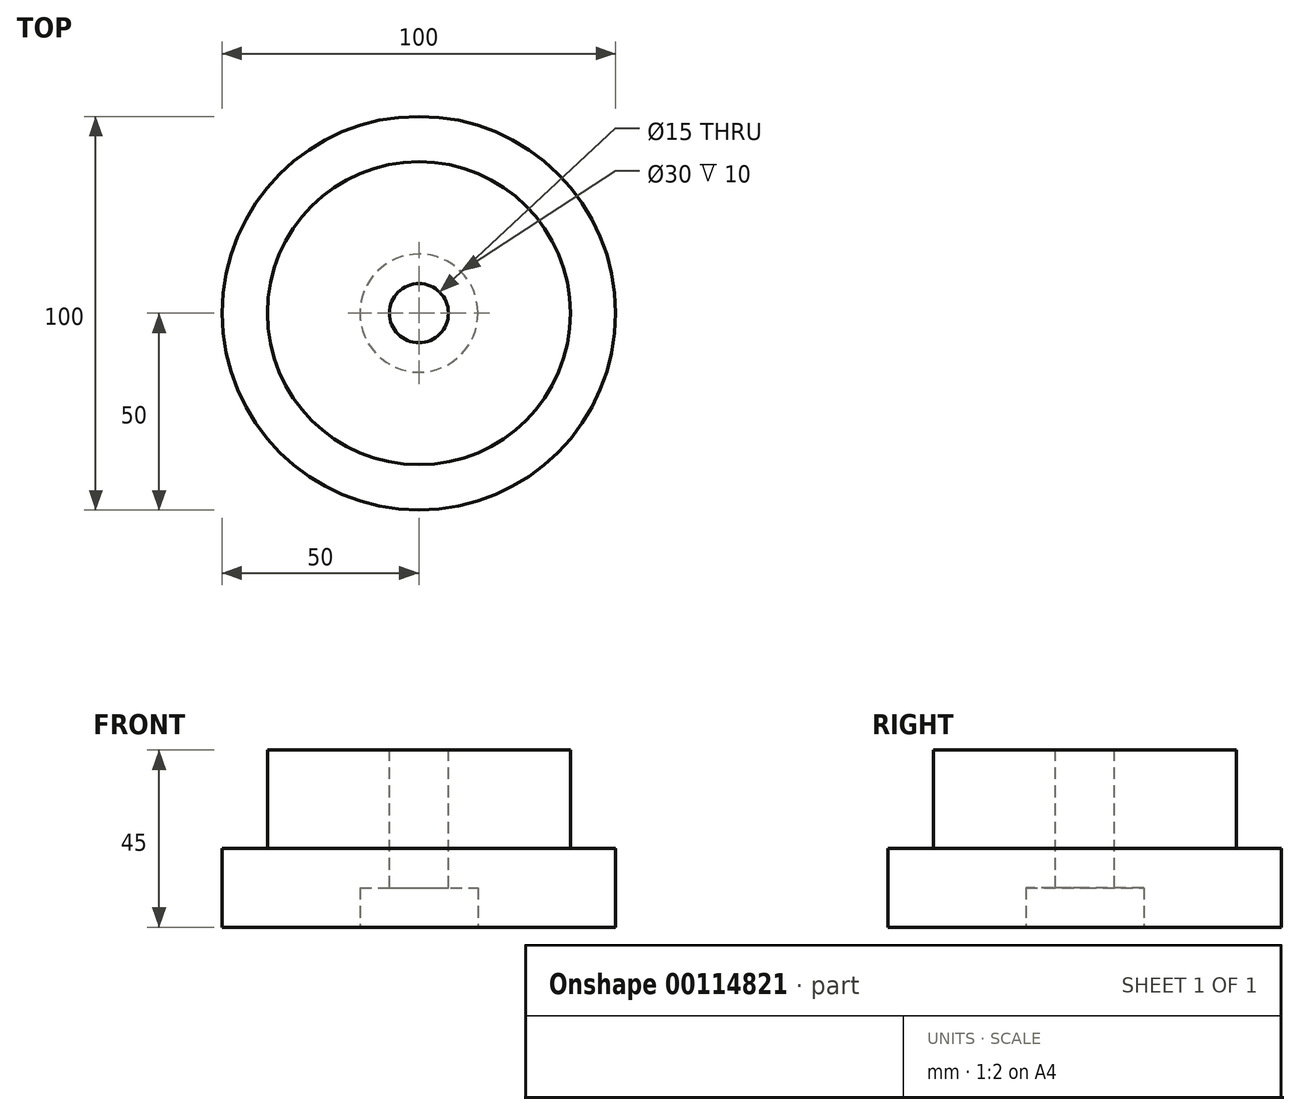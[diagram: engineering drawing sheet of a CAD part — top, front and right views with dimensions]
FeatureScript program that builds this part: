
annotation { "Feature Type Name" : "Feature", "Feature Type Description" : "" }
export const myFeature = defineFeature(function(context is Context, id is Id, definition is map)
    precondition{}
    {
        {
            var Q0;
            Q0=qCreatedBy(makeId("Top.planeOp"),FACE);
            var sketch = newSketch(context, id + "F0", { "sketchPlane" : qUnion([Q0])});
            skCircle(sketch, "E0", {"center": v(0, 0) * mm, "radius": 50 * mm});
            skSolve(sketch);
        }
        {
            var Q0;
            Q0=makeQuery(id+"F0.imprint","IMPRINT",FACE,{"disambiguationData":[TD([[makeQuery(id+"F0.imprint","IMPRINT",EDGE,{"derivedFrom":sQuery(id+"F0.wireOp",EDGE,"E0")}),1.0]])]});
            extrude(context, id + "F1", {"entities" : qUnion([Q0]), "depth" : 20 * mm});
        }
        {
            var Q0;
            Q0=makeQuery(id+"F1.opExtrude","CAP_FACE",FACE,{"disambiguationData":[OSD([sQuery(id+"F0.wireOp",EDGE,"E0")])],"isStart":false});
            var sketch = newSketch(context, id + "F2", { "sketchPlane" : qUnion([Q0])});
            skCircle(sketch, "E1", {"center": v(0, 0) * mm, "radius": 38.5 * mm});
            skSolve(sketch);
        }
        {
            var Q0;
            Q0=makeQuery(id+"F2.imprint","IMPRINT",FACE,{"disambiguationData":[TD([[makeQuery(id+"F2.imprint","IMPRINT",EDGE,{"derivedFrom":sQuery(id+"F2.wireOp",EDGE,"E1")}),1.0]])]});
            extrude(context, id + "F3", {"entities" : qUnion([Q0]), "operationType" : NewBodyOperationType.ADD, "depth" : 25 * mm});
        }
        {
            var Q0;
            Q0=makeQuery(id+"F1.opExtrude","CAP_FACE",FACE,{"disambiguationData":[OSD([sQuery(id+"F0.wireOp",EDGE,"E0")])],"isStart":true});
            var sketch = newSketch(context, id + "F4", { "sketchPlane" : qUnion([Q0])});
            skSolve(sketch);
        }
        {
            var Q0;
            Q0=makeQuery(id+"F3.opExtrude","CAP_FACE",FACE,{"disambiguationData":[OSD([sQuery(id+"F2.wireOp",EDGE,"E1")])],"isStart":false});
            var sketch = newSketch(context, id + "F5", { "sketchPlane" : qUnion([Q0])});
            skCircle(sketch, "E2", {"center": v(0, 0) * mm, "radius": 7.5 * mm});
            skSolve(sketch);
        }
        {
            var Q0;
            Q0=makeQuery(id+"F5.imprint","IMPRINT",FACE,{"disambiguationData":[TD([[makeQuery(id+"F5.imprint","IMPRINT",EDGE,{"derivedFrom":sQuery(id+"F5.wireOp",EDGE,"E2")}),1.0]])]});
            extrude(context, id + "F6", {"entities" : qUnion([Q0]), "operationType" : NewBodyOperationType.REMOVE, "oppositeDirection" : true, "depth" : 50 * mm});
        }
        {
            var Q0;
            Q0=makeQuery(id+"F4.imprint","IMPRINT",FACE,{"disambiguationData":[TD([[makeQuery(id+"F4.imprint","IMPRINT",EDGE,{"derivedFrom":makeQuery(id+"F1.opExtrude","CAP_EDGE",EDGE,{"disambiguationData":[OSD([sQuery(id+"F0.wireOp",EDGE,"E0")])],"isStart":true})}),-1.0]])]});
            var sketch = newSketch(context, id + "F7", { "sketchPlane" : qUnion([Q0])});
            skCircle(sketch, "E3", {"center": v(0, 0) * mm, "radius": 15 * mm});
            skSolve(sketch);
        }
        {
            var Q0;
            Q0=makeQuery(id+"F7.imprint","IMPRINT",FACE,{"disambiguationData":[TD([[makeQuery(id+"F7.imprint","IMPRINT",EDGE,{"derivedFrom":sQuery(id+"F7.wireOp",EDGE,"E3")}),1.0]])]});
            extrude(context, id + "F8", {"entities" : qUnion([Q0]), "operationType" : NewBodyOperationType.REMOVE, "oppositeDirection" : true, "depth" : 10 * mm});
        }
    });
